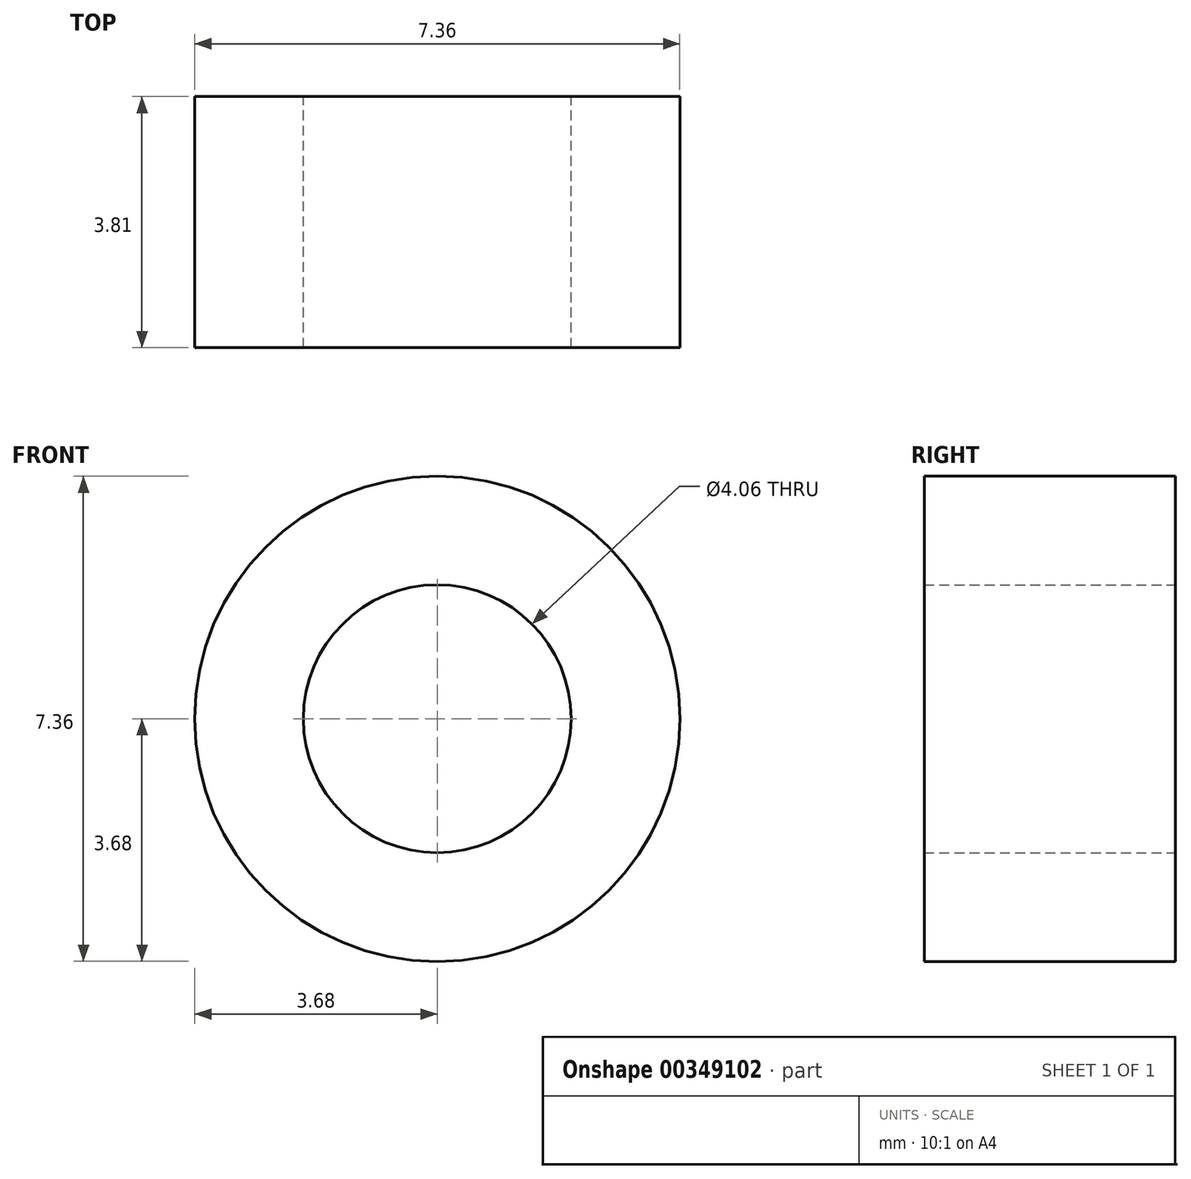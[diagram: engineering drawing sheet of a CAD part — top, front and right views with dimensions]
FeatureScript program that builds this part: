
annotation { "Feature Type Name" : "Feature", "Feature Type Description" : "" }
export const myFeature = defineFeature(function(context is Context, id is Id, definition is map)
    precondition{}
    {
        {
            var Q0;
            Q0=qCreatedBy(makeId("Front.planeOp"),FACE);
            var sketch = newSketch(context, id + "F0", { "sketchPlane" : qUnion([Q0])});
            skCircle(sketch, "E0", {"center": v(0, 0) * mm, "radius": 2.03 * mm});
            skCircle(sketch, "E1", {"center": v(0, 0) * mm, "radius": 3.68 * mm});
            skSolve(sketch);
        }
        {
            var Q0;
            Q0 = qSketchRegion(id + "F0", true);
            extrude(context, id + "F1", {"entities" : qUnion([Q0]), "depth" : 3.8 * mm});
        }
    });
